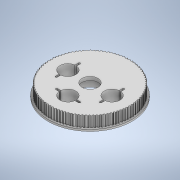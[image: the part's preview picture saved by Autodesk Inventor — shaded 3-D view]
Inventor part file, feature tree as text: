
AUTODESK INVENTOR PART (.ipt)
format: ipt  version: 2020.3 (Build 243373000, 373)  size: 1,094,656 bytes
history: native  units: mm
features: extrude x5, sketch x5, fillet x1
ambient origin geometry x8: Origin, YZ Plane, XZ Plane, XY Plane, X Axis, Y Axis, Z Axis, Center Point
bodies: Solid1 (feature_tree)
feature tree (11):
  extrude  "Extrusion1"  Depth=2.0mm TaperAngle=0.0deg
  extrude  "Extrusion2"  Depth=970.0mm TaperAngle=360.0deg
  extrude  "Extrusion3"  TaperAngle=0.0deg  [1 undecoded]
  extrude  "Extrusion4"  Depth=10.0mm TaperAngle=0.0deg
  extrude  "Extrusion5"  Depth=10.0mm TaperAngle=0.0deg
  fillet  "Fillet2"  Radius=1.0mm
  sketch  "Sketch1"  dims[d0=95.0mm d1=2.0mm d2=0.0mm]
  sketch  "Sketch2"  dims[d3=91.0mm d22=970.0mm d24=360.0deg]
  sketch  "Sketch3"  dims[d26=12.0mm d27=0.0mm d43=0.0mm d44=0.0mm]
  sketch  "Sketch5"  dims[d46=28.0mm d47=10.0mm d48=0.0mm]
  sketch  "Sketch6"  dims[d49=18.0mm d50=10.0mm d51=0.0mm d64=1.0mm d33=0.5mm d34=0.872665mm d35=0.5mm d36=0.872665mm]
note: 1 required parameter value undecoded (feature->parameter linkage not recoverable at this tier; creation-order binding heuristic only, values carry confidence <= 0.55)
